# Revit family: Power-ModularDevices-GEWISS-90AM-SWITCH_DISCONNECTOR_COMPACT
name_source: partatom
category: Apparecchi elettrici
revit_build: Autodesk Revit 2016 (Build: 20161004_0715(x64)
units: mm (PartAtom-declared; Revit-internal decimal feet)

## family parameters
Condiviso = No
Host = Superficie
Mantenere orientamento annotazione = Sì
Numero OmniClass = 23.80.50.00
Punto di calcolo locali = Sì
Quota connettore circolare = Usa diametro
Taglio con vuoti quando caricato = No
Tipo di parte = Normale
Titolo OmniClass = Terminals for Power Supply

## types (8) — shared parameters
Catalogue = POWER
Catalogue Range = 90 AM
Electrocod = 1422
IDF = ce60012e-9a15-4dd2-b63d-47a58cb0e9a0
IDT = b3914ede-b64d-4a60-9673-751a2c062d9d
Immagine tipo = GW96531.jpg
No. Chorus modules = 1
No. of modules EN 50022 = 1
Numero di poli = 1
Produttore = GEWISS S.p.A.
Prospetto di default = 1219 mm
SEO = Switch
Standard = EN 60669-2-4
Technical sheet = https://www.gewiss.com
URL = https://www.gewiss.com
Version file RFA = 18.0
carico = Altro
potenza in watt = 0 V
tipo = GENERICO - 90AM SEZIONATORI COMPATTI : GW96538

## per-type parameters (varying)
| type | Descrizione | EAN code | Modello | No. of poles | Number of poles | Rated current (In) | Rated current: | Rated voltage |
| GW96538 - COMP. ISOL. SWITCH 4P 32A 250-415V - 1 M | COMP. ISOL. SWITCH 4P 32A 250-415V - 1 M | 8011564447882 | GW96538 | 4P | 4P | 32A | 32A | 250-415V |
| GW96537 - COMP. ISOL. SWITCH 4P 16A 250-415V - 1 M | COMP. ISOL. SWITCH 4P 16A 250-415V - 1 M | 8011564447875 | GW96537 | 4P | 4P | 16A | 16A | 250-415V |
| GW96533 - COMP. ISOL. SWITCH 2P 16A 250-415V - 1 M | COMP. ISOL. SWITCH 2P 16A 250-415V - 1 M | 8011564447721 | GW96533 | 2P | 2P | 16A | 16A | 250-415V |
| GW96535 - COMP. ISOL. SWITCH 3P 16A 250-415V - 1 M | COMP. ISOL. SWITCH 3P 16A 250-415V - 1 M | 8011564448537 | GW96535 | 3P | 3P | 16A | 16A | 250-415V |
| GW96531 - COMP. ISOL. SWITCH 1P 16A 250V - 1 M | COMP. ISOL. SWITCH 1P 16A 250V - 1 M | 8011564447707 | GW96531 | 1P | 1P | 16A | 16A | 250V |
| GW96534 - COMP. ISOL. SWITCH 2P 32A 250-415V - 1 M | COMP. ISOL. SWITCH 2P 32A 250-415V - 1 M | 8011564447738 | GW96534 | 2P | 2P | 32A | 32A | 250-415V |
| GW96536 - COMP. ISOL. SWITCH 3P 32A 250-415V - 1 M | COMP. ISOL. SWITCH 3P 32A 250-415V - 1 M | 8011564447868 | GW96536 | 3P | 3P | 32A | 32A | 250-415V |
| GW96532 - COMP. ISOL. SWITCH 1P 32A 250V - 1 M | COMP. ISOL. SWITCH 1P 32A 250V - 1 M | 8011564447714 | GW96532 | 1P | 1P | 32A | 32A | 250V |
